# Revit family: NBS_PineappleContracts_GnrlFitngsFrnshngsAndEqpmntSym_RynoBedWithoutStorage
name_source: partatom
category: Furniture
revit_build: Autodesk Revit 2018 (Build: 20190510_1515(x64)
units: mm (PartAtom-declared; Revit-internal decimal feet)

## family parameters
Always vertical = Yes
Cut with Voids When Loaded = No
Room Calculation Point = No
Shared = No
Work Plane-Based = No

## types (1)
- RynoBedWithoutStorage
    AssetType = Fixed
    BIMObjectName = NBS_PineappleContracts_GeneralFittingsFurnishingsAndEquipmentSystem_RynoBedWithoutStorage
    BedFrameMaterial = NBS_PineappleContracts_IconPurple
    BedMattressMaterial = NBS_Concept
    Category = Pr_40_50_06_77:Single beds
    CodePerformance = BS EN 16139: 2013 level 2, BS 5852:2006, UL94 HB flammability standards
    Color = Blaze orange, epic blue, icon purple, vegas yellow, cool green, black, thunder grey, moonwalk grey, lime green, granite
    Description = Ryno bed without storage
    DurationUnit = year
    Features = Flame retardant, anti-bacterial, fixing options available
    Height = 480 mm  [stored 1.5748 ft]
    IfcExportAs = IfcFurnitureType
    IfcExportType = BED
    IsBuiltIn = No
    Length = 2100 mm
    ManufacturerName = Pineapple Contracts
    ManufacturerURL = www.pineapplecontracts.com
    Material = UV stabilised polyethylene with anti-microbial additive
    ModelNumber = ARYB-001
    ModelReference = RynoBedWithoutStorage
    NBSCertification = www.nationalbimlibrary.com/cert/wcokv0w4
    NBSDescription = General fittings, furnishings and equipment system
    NBSReference = 35-05-35/135
    Name = GeneralFittingsFurnishingsAndEquipmentSystem_RynoBedWithoutStorage_PineappleContracts
    NominalDepth = 0 mm  [stored 0 ft]
    NominalHeight = 480 mm  [stored 1.5748 ft]
    NominalLength = 2100 mm
    NominalWidth = 1010 mm  [stored 3.31365 ft]
    ProductInformation = https://uk.pineapplecontracts.com
    Shape = Rectangle
    Size = 480 x 2100 x 1010 mm
    Status = UNSET
    Style = Bed
    SustainabilityPerformance = 100% recyclable
    SystemManufacturer = Pineapple Contracts
    Uniclass2015Code = Pr_40_50_06_77
    Uniclass2015Title = Single beds
    Uniclass2015Version = Systems v1.15
    Version = 2
    WarrantyDescription = Lifetime guarantee against manufacturing faults
    WarrantyDurationUnit = year
    Weight = 90 kg standard
    Width = 1010 mm  [stored 3.31365 ft]

note: [stored X ft] marks values corroborated as IEEE doubles in the binary element streams (Revit-internal decimal feet)

## geometry (parser evidence)
native form markers: Sweep x2
no freeform markers — native parametric forms only
